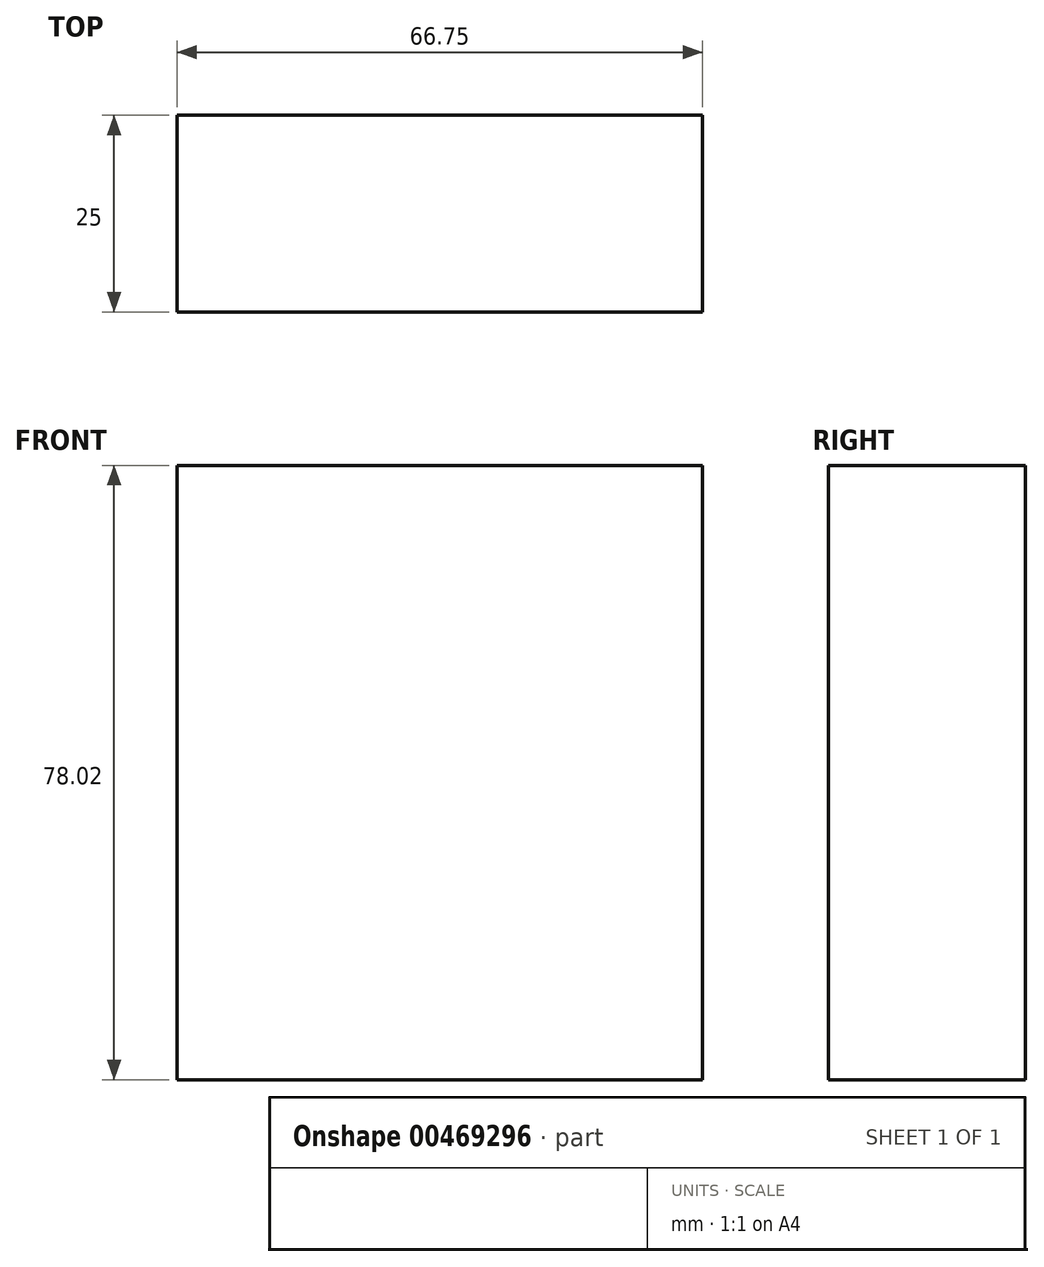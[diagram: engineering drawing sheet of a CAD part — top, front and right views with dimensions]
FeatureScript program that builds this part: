
annotation { "Feature Type Name" : "Feature", "Feature Type Description" : "" }
export const myFeature = defineFeature(function(context is Context, id is Id, definition is map)
    precondition{}
    {
        {
            var Q0;
            Q0=qCreatedBy(makeId("Front.planeOp"),FACE);
            var sketch = newSketch(context, id + "F0", { "sketchPlane" : qUnion([Q0])});
            skLineSegment(sketch, "E0.bottom", {"start": v(-108.81, 13.65) * mm, "end": v(-42.06, 13.65) * mm});
            skLineSegment(sketch, "E0.top", {"start": v(-108.81, 91.67) * mm, "end": v(-42.06, 91.67) * mm});
            skLineSegment(sketch, "E0.left", {"start": v(-108.81, 13.65) * mm, "end": v(-108.81, 91.67) * mm});
            skLineSegment(sketch, "E0.right", {"start": v(-42.06, 13.65) * mm, "end": v(-42.06, 91.67) * mm});
            skPoint(sketch, "E0.middle", {"position": v(-75.44, 52.66) * mm});
            skSolve(sketch);
        }
        {
            var Q0;
            Q0=makeQuery(id+"F0.imprint","IMPRINT",FACE,{"disambiguationData":[TD([[makeQuery(id+"F0.imprint","IMPRINT",EDGE,{"derivedFrom":sQuery(id+"F0.wireOp",EDGE,"E0.bottom")}),1.0]])]});
            extrude(context, id + "F1", {"entities" : qUnion([Q0]), "depth" : 25 * mm});
        }
    });
